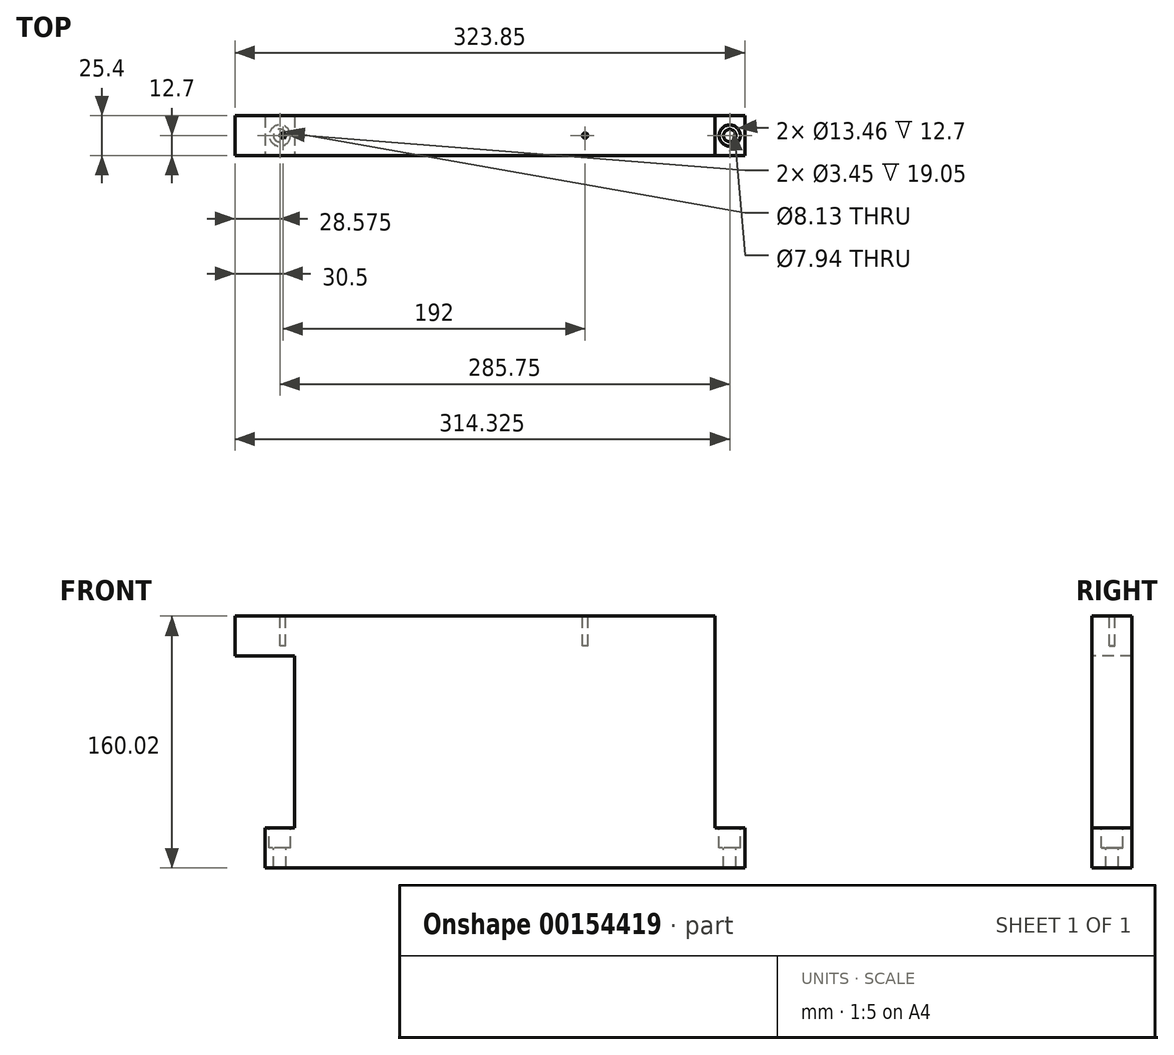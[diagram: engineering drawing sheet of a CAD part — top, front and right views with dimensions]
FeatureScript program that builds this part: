
annotation { "Feature Type Name" : "Feature", "Feature Type Description" : "" }
export const myFeature = defineFeature(function(context is Context, id is Id, definition is map)
    precondition{}
    {
        {
            var Q0;
            Q0=qCreatedBy(makeId("Top.planeOp"),FACE);
            var sketch = newSketch(context, id + "F0", { "sketchPlane" : qUnion([Q0])});
            skLineSegment(sketch, "E0.bottom", {"start": v(-152.4, 12.7) * mm, "end": v(152.4, 12.7) * mm});
            skLineSegment(sketch, "E0.top", {"start": v(-152.4, -12.7) * mm, "end": v(152.4, -12.7) * mm});
            skLineSegment(sketch, "E0.left", {"start": v(-152.4, 12.7) * mm, "end": v(-152.4, -12.7) * mm});
            skLineSegment(sketch, "E0.right", {"start": v(152.4, 12.7) * mm, "end": v(152.4, -12.7) * mm});
            skLineSegment(sketch, "E1", {"start": v(-152.4, 12.7) * mm, "end": v(152.4, -12.7) * mm, "construction": true});
            skSolve(sketch);
        }
        {
            var Q0;
            Q0=makeQuery(id+"F0.imprint","IMPRINT",FACE,{"disambiguationData":[TD([[makeQuery(id+"F0.imprint","IMPRINT",EDGE,{"derivedFrom":sQuery(id+"F0.wireOp",EDGE,"E0.bottom")}),-1.0]])]});
            extrude(context, id + "F1", {"entities" : qUnion([Q0]), "depth" : 160.02 * mm});
        }
        {
            var Q0;
            Q0=makeQuery(id+"F1.opExtrude","CAP_FACE",FACE,{"disambiguationData":[OSD([sQuery(id+"F0.wireOp",EDGE,"E0.bottom"),sQuery(id+"F0.wireOp",EDGE,"E0.top"),sQuery(id+"F0.wireOp",EDGE,"E0.left"),sQuery(id+"F0.wireOp",EDGE,"E0.right")])],"isStart":false});
            var sketch = newSketch(context, id + "F2", { "sketchPlane" : qUnion([Q0])});
            skLineSegment(sketch, "E2.bottom", {"start": v(-152.4, 12.7) * mm, "end": v(-133.35, 12.7) * mm});
            skLineSegment(sketch, "E2.top", {"start": v(-152.4, -12.7) * mm, "end": v(-133.35, -12.7) * mm});
            skLineSegment(sketch, "E2.left", {"start": v(-152.4, 12.7) * mm, "end": v(-152.4, -12.7) * mm});
            skLineSegment(sketch, "E2.right", {"start": v(-133.35, 12.7) * mm, "end": v(-133.35, -12.7) * mm});
            skLineSegment(sketch, "E3.bottom", {"start": v(152.4, 12.7) * mm, "end": v(133.35, 12.7) * mm});
            skLineSegment(sketch, "E3.top", {"start": v(152.4, -12.7) * mm, "end": v(133.35, -12.7) * mm});
            skLineSegment(sketch, "E3.left", {"start": v(152.4, 12.7) * mm, "end": v(152.4, -12.7) * mm});
            skLineSegment(sketch, "E3.right", {"start": v(133.35, 12.7) * mm, "end": v(133.35, -12.7) * mm});
            skSolve(sketch);
        }
        {
            var Q0;
            Q0=makeQuery(id+"F2.imprint","IMPRINT",FACE,{"disambiguationData":[TD([[makeQuery(id+"F2.imprint","IMPRINT",EDGE,{"derivedFrom":sQuery(id+"F2.wireOp",EDGE,"E2.bottom")}),-1.0]])]});
            var Q1;
            Q1=makeQuery(id+"F2.imprint","IMPRINT",FACE,{"disambiguationData":[TD([[makeQuery(id+"F2.imprint","IMPRINT",EDGE,{"derivedFrom":sQuery(id+"F2.wireOp",EDGE,"E3.bottom")}),-1.0]])]});
            extrude(context, id + "F3", {"entities" : qUnion([Q0, Q1]), "operationType" : NewBodyOperationType.REMOVE, "oppositeDirection" : true, "depth" : 134.62 * mm});
        }
        {
            var Q0;
            Q0=makeQuery(id+"F3.boolean.opBoolean","COPY",FACE,{"derivedFrom":makeQuery(id+"F3.opExtrude","CAP_FACE",FACE,{"disambiguationData":[OSD([sQuery(id+"F2.wireOp",EDGE,"E2.bottom"),sQuery(id+"F2.wireOp",EDGE,"E2.top"),sQuery(id+"F2.wireOp",EDGE,"E2.left"),sQuery(id+"F2.wireOp",EDGE,"E2.right")])],"isStart":false})});
            var sketch = newSketch(context, id + "F4", { "sketchPlane" : qUnion([Q0])});
            skLineSegment(sketch, "E4", {"start": v(-152.4, 0) * mm, "end": v(152.67, 0) * mm, "construction": true});
            skPoint(sketch, "E5.centerSnap0", {"position": v(-142.87, 12.7) * mm});
            skLineSegment(sketch, "E6", {"start": v(142.88, 12.65) * mm, "end": v(142.88, -13.08) * mm, "construction": true});
            skLineSegment(sketch, "E7", {"start": v(0, 13.08) * mm, "end": v(0, -12.43) * mm, "construction": true});
            skLineSegment(sketch, "E8", {"start": v(-142.88, 12.7) * mm, "end": v(-142.88, -12.7) * mm, "construction": true});
            skCircle(sketch, "E9", {"center": v(-142.88, 0) * mm, "radius": 4.06 * mm});
            skCircle(sketch, "E10", {"center": v(-142.88, 0) * mm, "radius": 6.73 * mm});
            skCircle(sketch, "E11", {"center": v(142.88, 0) * mm, "radius": 3.97 * mm});
            skCircle(sketch, "E12", {"center": v(142.88, 0) * mm, "radius": 6.73 * mm});
            skSolve(sketch);
        }
        {
            var Q0;
            Q0=makeQuery(id+"F4.imprint","IMPRINT",FACE,{"disambiguationData":[TD([[makeQuery(id+"F4.imprint","IMPRINT",EDGE,{"derivedFrom":sQuery(id+"F4.wireOp",EDGE,"E11")}),1.0]])]});
            var Q1;
            Q1=makeQuery(id+"F4.imprint","IMPRINT",FACE,{"disambiguationData":[TD([[makeQuery(id+"F4.imprint","IMPRINT",EDGE,{"derivedFrom":sQuery(id+"F4.wireOp",EDGE,"E9")}),1.0]])]});
            extrude(context, id + "F5", {"entities" : qUnion([Q0, Q1]), "operationType" : NewBodyOperationType.REMOVE, "endBound" : BoundingType.THROUGH_ALL, "oppositeDirection" : true, "depth" : 25.4 * mm});
        }
        {
            var Q0;
            Q0=qSketchRegion(id+"F4",true);
            extrude(context, id + "F6", {"entities" : qUnion([Q0]), "operationType" : NewBodyOperationType.REMOVE, "oppositeDirection" : true, "depth" : 12.7 * mm});
        }
        {
            var Q0;
            Q0=makeQuery(id+"F3.boolean.opBoolean","COPY",FACE,{"derivedFrom":makeQuery(id+"F3.opExtrude","SWEPT_FACE",FACE,{"disambiguationData":[OSD([sQuery(id+"F2.wireOp",EDGE,"E2.right")])]})});
            var sketch = newSketch(context, id + "F7", { "sketchPlane" : qUnion([Q0])});
            skLineSegment(sketch, "E13.bottom", {"start": v(-12.7, 160.02) * mm, "end": v(12.7, 160.02) * mm});
            skLineSegment(sketch, "E13.top", {"start": v(-12.7, 134.62) * mm, "end": v(12.7, 134.62) * mm});
            skLineSegment(sketch, "E13.left", {"start": v(-12.7, 160.02) * mm, "end": v(-12.7, 134.62) * mm});
            skLineSegment(sketch, "E13.right", {"start": v(12.7, 160.02) * mm, "end": v(12.7, 134.62) * mm});
            skSolve(sketch);
        }
        {
            var Q0;
            Q0=makeQuery(id+"F7.imprint","IMPRINT",FACE,{"disambiguationData":[TD([[makeQuery(id+"F7.imprint","IMPRINT",EDGE,{"derivedFrom":sQuery(id+"F7.wireOp",EDGE,"E13.bottom")}),-1.0]])]});
            extrude(context, id + "F8", {"entities" : qUnion([Q0]), "operationType" : NewBodyOperationType.ADD, "depth" : 38.1 * mm});
        }
        {
            var Q0;
            Q0=makeQuery(id+"F8.boolean.opBoolean","MERGE",FACE,{"derivedFrom":[makeQuery(id+"F1.opExtrude","CAP_FACE",FACE,{"disambiguationData":[OSD([sQuery(id+"F0.wireOp",EDGE,"E0.bottom"),sQuery(id+"F0.wireOp",EDGE,"E0.top"),sQuery(id+"F0.wireOp",EDGE,"E0.left"),sQuery(id+"F0.wireOp",EDGE,"E0.right")])],"isStart":false}),makeQuery(id+"F8.opExtrude","SWEPT_FACE",FACE,{"disambiguationData":[OSD([sQuery(id+"F7.wireOp",EDGE,"E13.bottom")])]})]});
            var sketch = newSketch(context, id + "F9", { "sketchPlane" : qUnion([Q0])});
            skLineSegment(sketch, "E14", {"start": v(-140.95, 12.7) * mm, "end": v(-140.95, -12.7) * mm, "construction": true});
            skLineSegment(sketch, "E15", {"start": v(51.05, 12.7) * mm, "end": v(51.05, -12.7) * mm, "construction": true});
            skLineSegment(sketch, "E16", {"start": v(-171.45, 0) * mm, "end": v(152.45, 0) * mm, "construction": true});
            skPoint(sketch, "E16.endSnap0", {"position": v(133.35, 0) * mm});
            skCircle(sketch, "E17", {"center": v(-140.95, 0) * mm, "radius": 1.73 * mm});
            skCircle(sketch, "E18", {"center": v(51.05, 0) * mm, "radius": 1.73 * mm});
            skSolve(sketch);
        }
        {
            var Q0;
            Q0=makeQuery(id+"F9.imprint","IMPRINT",FACE,{"disambiguationData":[TD([[makeQuery(id+"F9.imprint","IMPRINT",EDGE,{"derivedFrom":sQuery(id+"F9.wireOp",EDGE,"E17")}),1.0]])]});
            var Q1;
            Q1=makeQuery(id+"F9.imprint","IMPRINT",FACE,{"disambiguationData":[TD([[makeQuery(id+"F9.imprint","IMPRINT",EDGE,{"derivedFrom":sQuery(id+"F9.wireOp",EDGE,"E18")}),1.0]])]});
            extrude(context, id + "F10", {"entities" : qUnion([Q0, Q1]), "operationType" : NewBodyOperationType.REMOVE, "oppositeDirection" : true, "depth" : 19.05 * mm});
        }
    });
